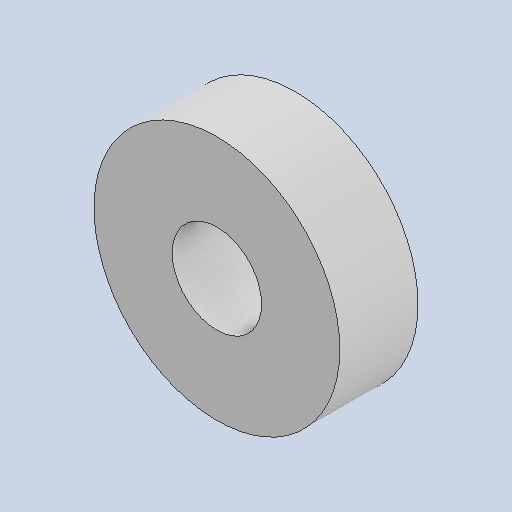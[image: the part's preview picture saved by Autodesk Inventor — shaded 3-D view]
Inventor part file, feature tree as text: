
AUTODESK INVENTOR PART (.ipt)
format: ipt  version: 2022 (Build 260153000, 153)  size: 92,672 bytes
history: native  units: in
note: dims shown in document units (in); Inventor stores cm internally (conversion verified against a paired STEP export)
features: other x3, sketch x1
ambient origin geometry x8: Origin, YZ Plane, XZ Plane, XY Plane, X Axis, Y Axis, Z Axis, Center Point
bodies: Solid1 (feature_tree)
feature tree (4):
  other  "608_MIR.ipt"
  other  "Solid1::608_MIR.ipt"
  other  "TaggingFeature1"
  sketch  "Sketch1"  dims[d0=0.3937in]
